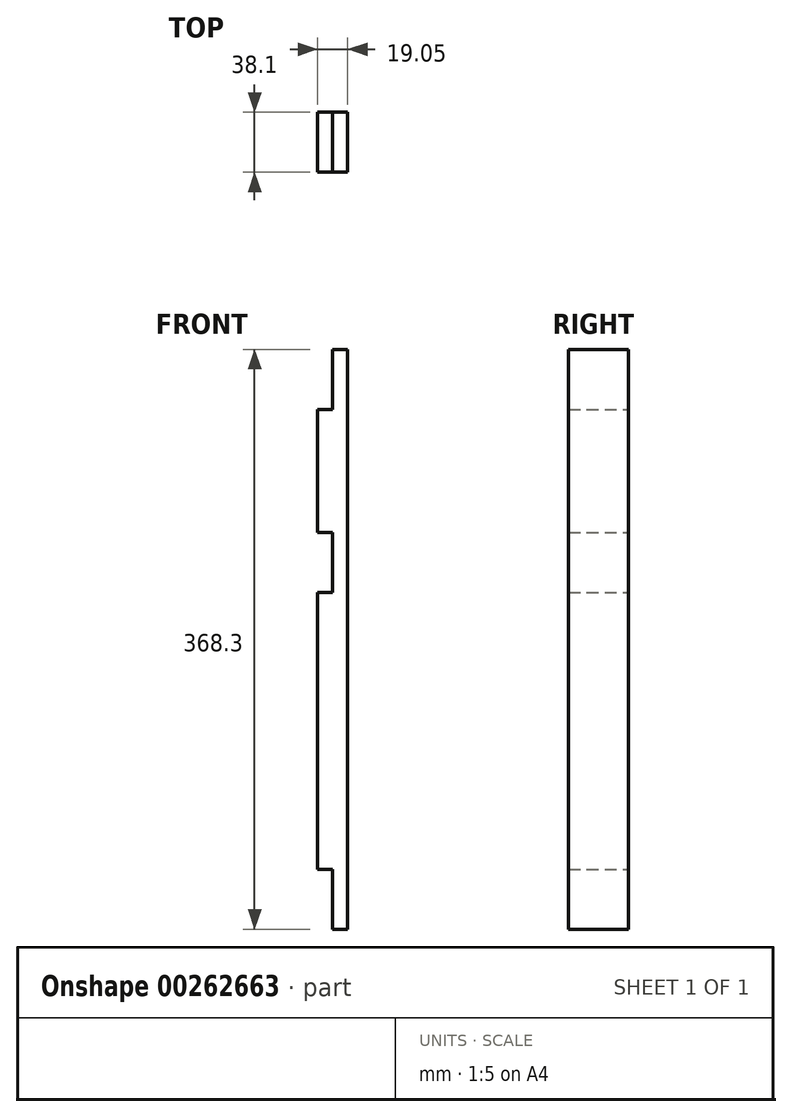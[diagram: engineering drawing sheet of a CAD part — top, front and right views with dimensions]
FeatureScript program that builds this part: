
annotation { "Feature Type Name" : "Feature", "Feature Type Description" : "" }
export const myFeature = defineFeature(function(context is Context, id is Id, definition is map)
    precondition{}
    {
        {
            var Q0;
            Q0=qCreatedBy(makeId("Front.planeOp"),FACE);
            var sketch = newSketch(context, id + "F0", { "sketchPlane" : qUnion([Q0])});
            skLineSegment(sketch, "E0", {"start": v(0, 0) * mm, "end": v(-9.53, 0) * mm});
            skLineSegment(sketch, "E1", {"start": v(-9.53, 0) * mm, "end": v(-9.53, -38.1) * mm});
            skLineSegment(sketch, "E2", {"start": v(-9.53, -38.1) * mm, "end": v(-19.05, -38.1) * mm});
            skLineSegment(sketch, "E3", {"start": v(-19.05, -38.1) * mm, "end": v(-19.05, -116.4) * mm});
            skLineSegment(sketch, "E4", {"start": v(-19.05, -116.4) * mm, "end": v(-9.52, -116.4) * mm});
            skLineSegment(sketch, "E5", {"start": v(-9.53, -116.4) * mm, "end": v(-9.53, -154.5) * mm});
            skLineSegment(sketch, "E6", {"start": v(-9.52, -154.5) * mm, "end": v(-19.05, -154.5) * mm});
            skLineSegment(sketch, "E7", {"start": v(-19.05, -330.2) * mm, "end": v(-9.52, -330.2) * mm});
            skLineSegment(sketch, "E8", {"start": v(-9.53, -330.2) * mm, "end": v(-9.53, -368.3) * mm});
            skLineSegment(sketch, "E9", {"start": v(-9.52, -368.3) * mm, "end": v(0, -368.3) * mm});
            skLineSegment(sketch, "E10", {"start": v(0, -368.3) * mm, "end": v(0, 0) * mm});
            skLineSegment(sketch, "E11", {"start": v(-19.05, -154.5) * mm, "end": v(-19.05, -330.2) * mm});
            skSolve(sketch);
        }
        {
            var Q0;
            Q0=makeQuery(id+"F0.imprint","IMPRINT",FACE,{"disambiguationData":[TD([[makeQuery(id+"F0.imprint","IMPRINT",EDGE,{"derivedFrom":sQuery(id+"F0.wireOp",EDGE,"E0")}),1.0]])]});
            extrude(context, id + "F1", {"entities" : qUnion([Q0]), "depth" : 38.1 * mm});
        }
    });
